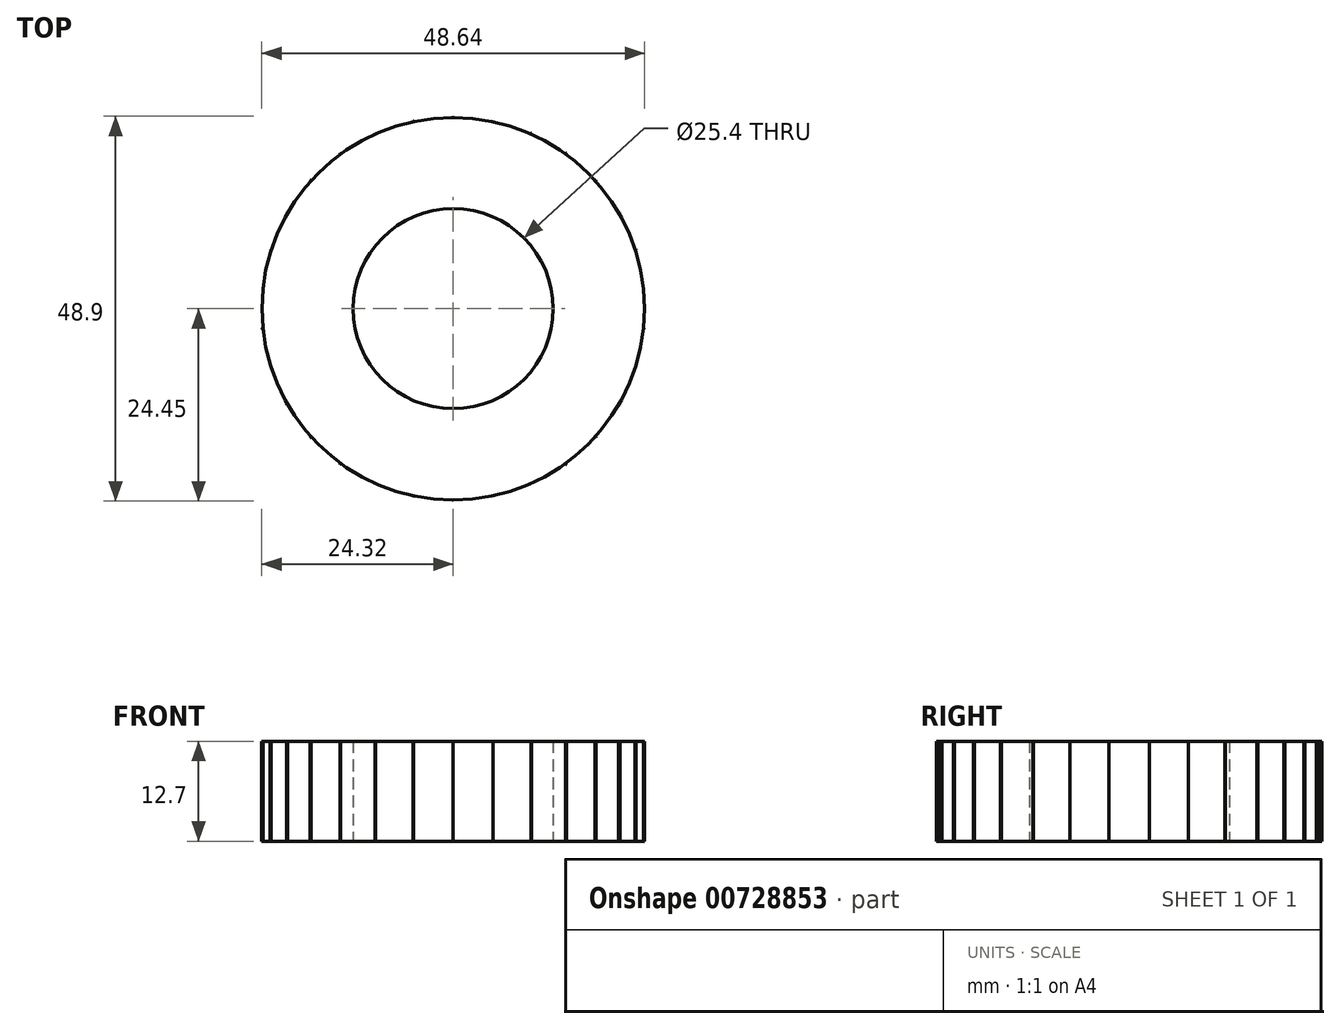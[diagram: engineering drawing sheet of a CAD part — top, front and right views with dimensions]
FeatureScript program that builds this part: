
annotation { "Feature Type Name" : "Feature", "Feature Type Description" : "" }
export const myFeature = defineFeature(function(context is Context, id is Id, definition is map)
    precondition{}
    {
        {
            var Q0;
            Q0=qCreatedBy(makeId("Top.planeOp"),FACE);
            var sketch = newSketch(context, id + "F0", { "sketchPlane" : qUnion([Q0])});
            skCircle(sketch, "E0", {"center": v(0, 0) * mm, "radius": 26.67 * mm, "construction": true});
            skCircle(sketch, "E1", {"center": v(0, 0) * mm, "radius": 24.29 * mm});
            skCircle(sketch, "E2", {"center": v(0, 0) * mm, "radius": 26.07 * mm, "construction": true});
            skCircle(sketch, "E3", {"center": v(0, 0) * mm, "radius": 24.5 * mm, "construction": true});
            skCircle(sketch, "E4", {"center": v(0, 0) * mm, "radius": 12.7 * mm});
            skSolve(sketch);
        }
        {
            var Q0;
            Q0=qCreatedBy(makeId("Top.planeOp"),FACE);
            var sketch = newSketch(context, id + "F1", { "sketchPlane" : qUnion([Q0])});
            skCircle(sketch, "E5.0", {"center": v(0, 0) * mm, "radius": 24.5 * mm, "construction": true});
            skLineSegment(sketch, "E6", {"start": v(0, 0) * mm, "end": v(0, 24.5) * mm, "construction": true});
            skLineSegment(sketch, "E7.1.0", {"start": v(0, 0) * mm, "end": v(-5.45, 23.88) * mm, "construction": true});
            skLineSegment(sketch, "E7.2.0", {"start": v(0, 0) * mm, "end": v(-10.63, 22.07) * mm, "construction": true});
            skLineSegment(sketch, "E7.3.0", {"start": v(0, 0) * mm, "end": v(-15.27, 19.15) * mm, "construction": true});
            skLineSegment(sketch, "E7.4.0", {"start": v(0, 0) * mm, "end": v(-19.15, 15.27) * mm, "construction": true});
            skLineSegment(sketch, "E7.5.0", {"start": v(0, 0) * mm, "end": v(-22.07, 10.63) * mm, "construction": true});
            skLineSegment(sketch, "E7.6.0", {"start": v(0, 0) * mm, "end": v(-23.88, 5.45) * mm, "construction": true});
            skLineSegment(sketch, "E7.7.0", {"start": v(0, 0) * mm, "end": v(-24.5, 0) * mm, "construction": true});
            skLineSegment(sketch, "E7.anchor2", {"start": v(0, 0) * mm, "end": v(-24.5, 0) * mm, "construction": true});
            skLineSegment(sketch, "E8", {"start": v(-5.45, 23.88) * mm, "end": v(-0.15, 25.1) * mm, "construction": true});
            skLineSegment(sketch, "E9", {"start": v(-10.63, 22.07) * mm, "end": v(-0.83, 26.8) * mm, "construction": true});
            skLineSegment(sketch, "E10", {"start": v(-15.27, 19.15) * mm, "end": v(-2.52, 29.33) * mm, "construction": true});
            skLineSegment(sketch, "E11", {"start": v(-19.15, 15.27) * mm, "end": v(-5.59, 32.28) * mm, "construction": true});
            skCircle(sketch, "E12.0", {"center": v(0, 0) * mm, "radius": 26.67 * mm});
            skSolve(sketch);
        }
        {
            var Q0;
            Q0=qCreatedBy(makeId("Top.planeOp"),FACE);
            var sketch = newSketch(context, id + "F2", { "sketchPlane" : qUnion([Q0])});
            skCircle(sketch, "E13.0", {"center": v(0, 0) * mm, "radius": 24.29 * mm});
            skCircle(sketch, "E14.0", {"center": v(0, 0) * mm, "radius": 24.5 * mm, "construction": true});
            skLineSegment(sketch, "E15.0", {"start": v(-19.15, 15.27) * mm, "end": v(-5.59, 32.28) * mm, "construction": true});
            skLineSegment(sketch, "E15.1", {"start": v(-15.27, 19.15) * mm, "end": v(-2.52, 29.33) * mm, "construction": true});
            skLineSegment(sketch, "E15.2", {"start": v(-10.63, 22.07) * mm, "end": v(-0.83, 26.8) * mm, "construction": true});
            skLineSegment(sketch, "E15.3", {"start": v(-5.45, 23.88) * mm, "end": v(-0.15, 25.1) * mm, "construction": true});
            skLineSegment(sketch, "E16", {"start": v(0, 24.5) * mm, "end": v(0, 24.29) * mm});
            skLineSegment(sketch, "E17", {"start": v(0, 0) * mm, "end": v(-1.36, 24.46) * mm, "construction": true});
            skLineSegment(sketch, "E18.0", {"start": v(0, 0) * mm, "end": v(-5.45, 23.88) * mm, "construction": true});
            skLineSegment(sketch, "E19.0", {"start": v(0, 0) * mm, "end": v(0, 24.29) * mm, "construction": true});
            skFitSpline(sketch, "E20", {"points": [v(0, 24.5) * mm, v(-0.15, 25.1) * mm, v(-0.83, 26.8) * mm, v(-2.52, 29.33) * mm, v(-5.59, 32.28) * mm], "startDerivative": vector(-0.02, 4.07) * mm, "endDerivative": vector(-8.45, 9.56) * mm});
            skFitSpline(sketch, "E21.MirrorCS", {"points": [v(-2.72, 24.35) * mm, v(-2.64, 24.96) * mm, v(-2.15, 26.72) * mm, v(-0.76, 29.43) * mm, v(1.97, 32.7) * mm], "startDerivative": vector(-0.43, 4.05) * mm, "endDerivative": vector(7.33, 10.44) * mm});
            skLineSegment(sketch, "E22.MirrorCS", {"start": v(-2.72, 24.35) * mm, "end": v(-2.7, 24.14) * mm});
            skSolve(sketch);
        }
        {
            var Q0;
            {var subQ4=sQuery(id+"F2.wireOp",EDGE,"E16");Q0=makeQuery(id+"F2.imprint","IMPRINT",FACE,{"disambiguationData":[TD([[makeQuery(id+"F2.imprint","IMPRINT",EDGE,{"derivedFrom":subQ4}),-1.0]])]});}
            var sketch = newSketch(context, id + "F3", { "sketchPlane" : qUnion([Q0])});
            skPoint(sketch, "E23.orphan", {"position": v(-1.57, 28.11) * mm});
            skPoint(sketch, "E24.orphan", {"position": v(-5.45, 23.88) * mm});
            skPoint(sketch, "E25.0.1.start.orphan", {"position": v(-2.72, 24.35) * mm});
            skPoint(sketch, "E25.0.3.start.orphan", {"position": v(0, 24.29) * mm});
            skPoint(sketch, "E26.orphan", {"position": v(-2.7, 24.14) * mm});
            skFitSpline(sketch, "E27.0.0", {"points": [v(1.8, 32.56) * mm, v(0.94, 31.35) * mm, v(-1.04, 29.45) * mm, v(-2.28, 26.68) * mm, v(-2.7, 24.8) * mm, v(-2.74, 24.31) * mm, v(-2.72, 24.14) * mm]});
            skLineSegment(sketch, "E27.0.1", {"start": v(-2.72, 24.35) * mm, "end": v(-2.7, 24.14) * mm});
            skArc(sketch, "E27.0.2", {"start": v(-2.7, 24.14) * mm, "mid": v(-1.35, 24.25) * mm, "end": v(0, 24.29) * mm});
            skLineSegment(sketch, "E27.0.3", {"start": v(0, 24.29) * mm, "end": v(0, 24.5) * mm});
            skFitSpline(sketch, "E27.0.4", {"points": [v(0, 24.29) * mm, v(0, 24.47) * mm, v(-0.1, 24.95) * mm, v(-0.72, 26.76) * mm, v(-2.26, 29.38) * mm, v(-4.45, 31.05) * mm, v(-5.43, 32.15) * mm]});
            skArc(sketch, "E28.0", {"start": v(-0.77, 26.66) * mm, "mid": v(-1.48, 26.63) * mm, "end": v(-2.2, 26.58) * mm});
            skSolve(sketch);
        }
        {
            var Q0;
            Q0 = qSketchRegion(id + "F3", true);
            extrude(context, id + "F4", {"entities" : qUnion([Q0]), "depth" : 12.7 * mm, "offsetDistance" : 25.4 * mm});
        }
        {
            var Q0;
            Q0=qCreatedBy(makeId("Front.planeOp"),FACE);
            var sketch = newSketch(context, id + "F5", { "sketchPlane" : qUnion([Q0])});
            skLineSegment(sketch, "E29", {"start": v(0, 18.92) * mm, "end": v(0, -7.98) * mm, "construction": true});
            skSolve(sketch);
        }
        {
            var Q0;
            Q0=makeQuery(id+"F0.imprint","IMPRINT",FACE,{"disambiguationData":[TD([[makeQuery(id+"F0.imprint","IMPRINT",EDGE,{"derivedFrom":sQuery(id+"F0.wireOp",EDGE,"E1")}),1.0]])]});
            extrude(context, id + "F6", {"entities" : qUnion([Q0]), "operationType" : NewBodyOperationType.ADD, "depth" : 12.7 * mm, "offsetDistance" : 25.4 * mm});
        }
        {
            var Q0;
            Q0=makeQuery(id+"F4.opExtrude","SWEPT_BODY",BODY,{"disambiguationData":[OSD([sQuery(id+"F3.wireOp",EDGE,"E27.0.0"),sQuery(id+"F3.wireOp",EDGE,"E27.0.1"),sQuery(id+"F3.wireOp",EDGE,"E27.0.2"),sQuery(id+"F3.wireOp",EDGE,"E27.0.3"),sQuery(id+"F3.wireOp",EDGE,"E27.0.4"),sQuery(id+"F3.wireOp",EDGE,"E28.0")])]});
            var Q1;
            Q1=sQuery(id+"F5.wireOp",EDGE,"E29");
            circularPattern(context, id + "F7", {"operationType" : NewBodyOperationType.ADD, "entities" : qUnion([Q0]), "axis" : qUnion([Q1]), "angle" : 360 * degree, "instanceCount" : 30, "equalSpace" : true});
        }
    });
